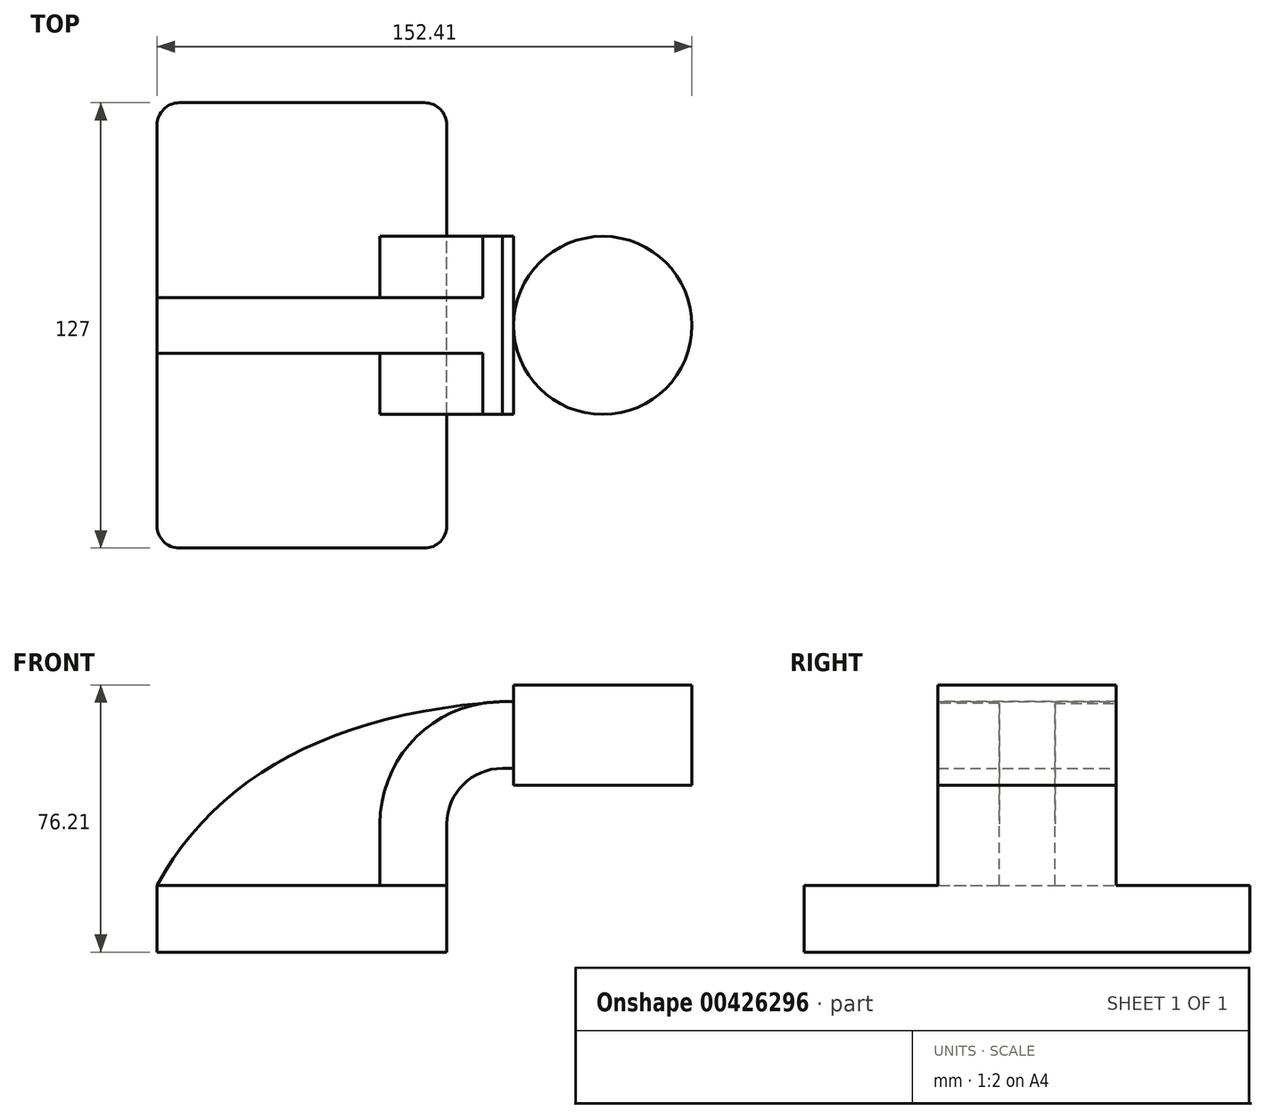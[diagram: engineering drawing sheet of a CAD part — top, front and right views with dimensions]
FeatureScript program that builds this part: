
annotation { "Feature Type Name" : "Feature", "Feature Type Description" : "" }
export const myFeature = defineFeature(function(context is Context, id is Id, definition is map)
    precondition{}
    {
        {
            var Q0;
            Q0=qCreatedBy(makeId("Front.planeOp"),FACE);
            var sketch = newSketch(context, id + "F0", { "sketchPlane" : qUnion([Q0])});
            skLineSegment(sketch, "E0.bottom", {"start": v(41.27, 9.53) * mm, "end": v(-41.28, 9.53) * mm});
            skLineSegment(sketch, "E0.top", {"start": v(41.28, -9.52) * mm, "end": v(-41.27, -9.52) * mm});
            skLineSegment(sketch, "E0.left", {"start": v(41.28, 9.53) * mm, "end": v(41.28, -9.52) * mm});
            skLineSegment(sketch, "E0.right", {"start": v(-41.28, 9.53) * mm, "end": v(-41.27, -9.52) * mm});
            skPoint(sketch, "E0.middle", {"position": v(0, 0) * mm});
            skLineSegment(sketch, "E1.bottom", {"start": v(111.12, 38.1) * mm, "end": v(60.32, 38.1) * mm});
            skLineSegment(sketch, "E1.top", {"start": v(111.12, 66.68) * mm, "end": v(60.32, 66.68) * mm});
            skLineSegment(sketch, "E1.left", {"start": v(111.12, 38.1) * mm, "end": v(111.12, 66.68) * mm});
            skLineSegment(sketch, "E1.right", {"start": v(60.32, 38.1) * mm, "end": v(60.32, 66.68) * mm});
            skPoint(sketch, "E1.middle", {"position": v(85.72, 52.39) * mm});
            skLineSegment(sketch, "E2", {"start": v(41.27, 9.53) * mm, "end": v(41.27, 27) * mm});
            skArc(sketch, "E3", {"start": v(41.27, 27) * mm, "mid": v(45.92, 38.23) * mm, "end": v(57.15, 42.88) * mm});
            skLineSegment(sketch, "E4", {"start": v(57.15, 42.88) * mm, "end": v(90.31, 42.88) * mm});
            skLineSegment(sketch, "E5.0", {"start": v(57.15, 61.93) * mm, "end": v(85.72, 61.93) * mm});
            skArc(sketch, "E5.1", {"start": v(22.23, 27) * mm, "mid": v(32.45, 51.7) * mm, "end": v(57.15, 61.93) * mm});
            skLineSegment(sketch, "E5.2", {"start": v(22.22, 9.53) * mm, "end": v(22.22, 27) * mm});
            skFitSpline(sketch, "E6", {"points": [v(-41.28, 9.53) * mm, v(57.15, 61.93) * mm], "startDerivative": vector(50.82, 94.1) * mm, "endDerivative": vector(144.96, 9.84) * mm});
            skLineSegment(sketch, "E7", {"start": v(85.72, 38.1) * mm, "end": v(85.72, 66.68) * mm});
            skSolve(sketch);
        }
        {
            var Q0;
            Q0=makeQuery(id+"F0.imprint","IMPRINT",FACE,{"disambiguationData":[TD([[makeQuery(id+"F0.imprint","IMPRINT",EDGE,{"derivedFrom":sQuery(id+"F0.wireOp",EDGE,"E0.top")}),-1.0]])]});
            extrude(context, id + "F1", {"entities" : qUnion([Q0]), "endBound" : BoundingType.SYMMETRIC, "depth" : 127 * mm});
        }
        {
            var Q0;
            {var subQ6=sQuery(id+"F0.wireOp",EDGE,"E2");Q0=makeQuery(id+"F0.imprint","IMPRINT",FACE,{"disambiguationData":[TD([[makeQuery(id+"F0.imprint","IMPRINT",EDGE,{"derivedFrom":subQ6}),1.0]])]});}
            extrude(context, id + "F2", {"entities" : qUnion([Q0]), "operationType" : NewBodyOperationType.ADD, "endBound" : BoundingType.SYMMETRIC, "depth" : 50.8 * mm});
        }
        {
            var Q0;
            {var subQ3=sQuery(id+"F0.wireOp",EDGE,"E5.2");Q0=makeQuery(id+"F0.imprint","IMPRINT",FACE,{"disambiguationData":[TD([[makeQuery(id+"F0.imprint","IMPRINT",EDGE,{"derivedFrom":subQ3}),1.0]])]});}
            extrude(context, id + "F3", {"entities" : qUnion([Q0]), "operationType" : NewBodyOperationType.ADD, "endBound" : BoundingType.SYMMETRIC, "depth" : 15.88 * mm});
        }
        {
            var Q0;
            {var subQ4=sQuery(id+"F0.wireOp",EDGE,"E1.left");Q0=makeQuery(id+"F0.imprint","IMPRINT",FACE,{"disambiguationData":[TD([[makeQuery(id+"F0.imprint","IMPRINT",EDGE,{"derivedFrom":subQ4}),1.0]])]});}
            var Q1;
            Q1=sQuery(id+"F0.wireOp",EDGE,"E7");
            revolve(context, id + "F4", {"operationType" : NewBodyOperationType.ADD, "entities" : qUnion([Q0]), "axis" : qUnion([Q1]), "revolveType" : RevolveType.FULL});
        }
        {
            var Q0;
            Q0=makeQuery(id+"F1.opExtrude","CAP_EDGE",EDGE,{"disambiguationData":[OSD([sQuery(id+"F0.wireOp",EDGE,"E0.right")])],"isStart":false});
            var Q1;
            Q1=makeQuery(id+"F1.opExtrude","CAP_EDGE",EDGE,{"disambiguationData":[OSD([sQuery(id+"F0.wireOp",EDGE,"E0.right")])],"isStart":true});
            var Q2;
            Q2=makeQuery(id+"F1.opExtrude","CAP_EDGE",EDGE,{"disambiguationData":[OSD([sQuery(id+"F0.wireOp",EDGE,"E0.left")])],"isStart":false});
            var Q3;
            Q3=makeQuery(id+"F1.opExtrude","CAP_EDGE",EDGE,{"disambiguationData":[OSD([sQuery(id+"F0.wireOp",EDGE,"E0.left")])],"isStart":true});
            fillet(context, id + "F5", {"entities" : qUnion([Q0, Q1, Q2, Q3]), "radius" : 6.35 * mm, "tangentPropagation" : true, "allowEdgeOverflow" : false});
        }
    });
